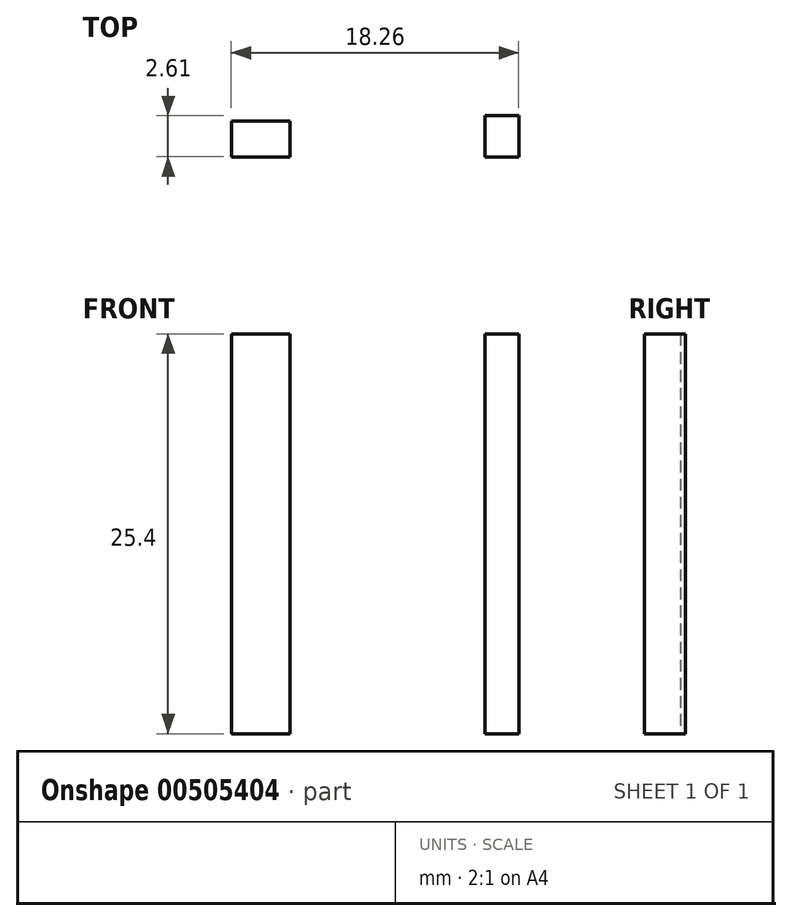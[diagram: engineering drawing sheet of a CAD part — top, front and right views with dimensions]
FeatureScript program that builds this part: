
annotation { "Feature Type Name" : "Feature", "Feature Type Description" : "" }
export const myFeature = defineFeature(function(context is Context, id is Id, definition is map)
    precondition{}
    {
        {
            var Q0;
            Q0=qCreatedBy(makeId("Top.planeOp"),FACE);
            var sketch = newSketch(context, id + "F0", { "sketchPlane" : qUnion([Q0])});
            skLineSegment(sketch, "E0.bottom", {"start": v(-80.03, 34.86) * mm, "end": v(32.7, 34.86) * mm});
            skLineSegment(sketch, "E0.top", {"start": v(-80.03, -4.81) * mm, "end": v(32.7, -4.81) * mm});
            skLineSegment(sketch, "E0.left", {"start": v(-80.03, 34.86) * mm, "end": v(-80.03, -4.81) * mm});
            skLineSegment(sketch, "E0.right", {"start": v(32.7, 34.86) * mm, "end": v(32.7, -4.81) * mm});
            skLineSegment(sketch, "E1.bottom", {"start": v(-83.28, 44.4) * mm, "end": v(-79.53, 44.4) * mm});
            skLineSegment(sketch, "E1.top", {"start": v(-83.28, 42.13) * mm, "end": v(-79.53, 42.13) * mm});
            skLineSegment(sketch, "E1.left", {"start": v(-83.28, 44.4) * mm, "end": v(-83.28, 42.13) * mm});
            skLineSegment(sketch, "E1.right", {"start": v(-79.53, 44.4) * mm, "end": v(-79.53, 42.13) * mm});
            skLineSegment(sketch, "E2.bottom", {"start": v(-67.17, 42.13) * mm, "end": v(-65.02, 42.13) * mm});
            skLineSegment(sketch, "E2.top", {"start": v(-67.17, 44.74) * mm, "end": v(-65.02, 44.74) * mm});
            skLineSegment(sketch, "E2.left", {"start": v(-67.17, 42.13) * mm, "end": v(-67.17, 44.74) * mm});
            skLineSegment(sketch, "E2.right", {"start": v(-65.02, 42.13) * mm, "end": v(-65.02, 44.74) * mm});
            skSolve(sketch);
        }
        {
            var Q0;
            Q0=makeQuery(id+"F0.imprint","IMPRINT",FACE,{"disambiguationData":[TD([[makeQuery(id+"F0.imprint","IMPRINT",EDGE,{"derivedFrom":sQuery(id+"F0.wireOp",EDGE,"E1.bottom")}),-1.0]])]});
            var Q1;
            Q1=makeQuery(id+"F0.imprint","IMPRINT",FACE,{"disambiguationData":[TD([[makeQuery(id+"F0.imprint","IMPRINT",EDGE,{"derivedFrom":sQuery(id+"F0.wireOp",EDGE,"E2.bottom")}),1.0]])]});
            extrude(context, id + "F1", {"entities" : qUnion([Q0, Q1]), "depth" : 25.4 * mm});
        }
    });
